# Revit family: RN 81041 Optipress-Aquaplus-Vis de rappel
name_source: partatom
category: Rohrformteile
units: mm (PartAtom-declared; Revit-internal decimal feet)

## family parameters
Arbeitsebenenbasiert = Nein
Beim Laden mit Abzugskörper schneiden = Nein
Bemaßung runder Anschluss = Durchmesser verwenden
Gemeinsam genutzt = Nein
Immer vertikal = Ja
Teiletyp = Verbindung

## types (7) — shared parameters
1.010.00.2 Numéro de feuille de la directive = 29
1.010.00.3 Date de publication (mois) de la ligne directrice = 201308
1.010.00.4 Nom du Fabricant = R. Nussbaum AG
1.010.00.5 Date de révision du fichier = 20190521
1.010.00.6 Adresse Web du fabricant = http://www.nussbaum.ch
1.100.00.4 Désignation du produit = Alimentation
1.110.00.2 Indice = 4
1.110.00.4 Désignation du produit = Optipress
1.960/3L.00.8 Lien (URL) = https://www.nussbaum.ch
29.700.00.4 Nom du produit = Optipress-Aquaplus-Vis de rappel
29.700.00.5 Identification du produit = 2
29.700.00.6 Forme transversale = 1
29.700.00.7 Système de taille nominale = DN
29.700.00.8 Système de pression nominale = PN
29.710.02.4 Pression nominale = 16
29.710.02.5 Max. [hPa] = 1600
29.710.02.7 Max. [hPa] = 1600
29.710.02.9 Max. [°C] = 95
Connector Visibility = Nein
EnclosingSpace Visibility = Nein

## per-type parameters (varying)
| type | 1.800.00.3 Numéro BS | 1.810.00.3 Numéro de commande fabricant | 1.810.00.4 Numéro DATANORM | 1.810.00.5 Numéro StLB | 1.810.00.6 Numéro GTIN | 29.710.02.10 Poids d'ajustement [kg] | 29.710.02.3 La désignation | CONNECTOR0_DIAMETER_dX_0r | CONNECTOR0_dX_01 | CONNECTOR0_ref_dX | CONNECTOR1_DIAMETER_dX_0r | CONNECTOR1_dX_00 | CONNECTOR1_dX_01 | CONNECTOR1_ref_dX | R. Nussbaum AG 81041.22 fr Visibility | R. Nussbaum AG 81041.23 fr Visibility | R. Nussbaum AG 81041.24 fr Visibility | R. Nussbaum AG 81041.25 fr Visibility | R. Nussbaum AG 81041.26 fr Visibility | R. Nussbaum AG 81041.27 fr Visibility | R. Nussbaum AG 81041.28 fr Visibility |
| 81041.22, Optipress-Aquaplus-Vis de rappel, DN=12, L=82 | 01900400000000000000000000000000000000000000000026000000000000000008 | 81041.22 | 81041.22 | 266.312 | 7612945021984 | 0.191 | Optipress-Aquaplus-Vis de rappel, DN=12, L=82 | 12 mm  [stored 0.0393701 ft] | 22 mm | 22 mm | 12 mm  [stored 0.0393701 ft] | 53 mm | 75 mm | 53 mm | Ja | Nein | Nein | Nein | Nein | Nein | Nein |
| 81041.23, Optipress-Aquaplus-Vis de rappel, DN=15, L=85 | 01900400000000000000000000000000000000000000000026000000000000000009 | 81041.23 | 81041.23 | 266.313 | 7612945021991 | 0.152 | Optipress-Aquaplus-Vis de rappel, DN=15, L=85 | 15 mm  [stored 0.0492126 ft] | 22 mm | 22 mm | 15 mm  [stored 0.0492126 ft] | 56 mm | 78 mm | 56 mm | Nein | Ja | Nein | Nein | Nein | Nein | Nein |
| 81041.24, Optipress-Aquaplus-Vis de rappel, DN=20, L=91 | 01900400000000000000000000000000000000000000000026000000000000000010 | 81041.24 | 81041.24 | 266.314 | 7612945022004 | 0.229 | Optipress-Aquaplus-Vis de rappel, DN=20, L=91 | 20 mm | 24 mm | 24 mm | 20 mm | 62 mm | 86 mm | 62 mm | Nein | Nein | Ja | Nein | Nein | Nein | Nein |
| 81041.25, Optipress-Aquaplus-Vis de rappel, DN=25, L=100 | 01900400000000000000000000000000000000000000000026000000000000000011 | 81041.25 | 81041.25 | 266.315 | 7612945022011 | 0.315 | Optipress-Aquaplus-Vis de rappel, DN=25, L=100 | 25 mm  [stored 0.082021 ft] | 24 mm | 24 mm | 25 mm  [stored 0.082021 ft] | 71 mm | 95 mm | 71 mm | Nein | Nein | Nein | Ja | Nein | Nein | Nein |
| 81041.26, Optipress-Aquaplus-Vis de rappel, DN=32, L=108 | 01900400000000000000000000000000000000000000000026000000000000000012 | 81041.26 | 81041.26 | 266.316 | 7612945022028 | 0.425 | Optipress-Aquaplus-Vis de rappel, DN=32, L=108 | 32 mm | 26 mm | 26 mm | 32 mm | 74 mm | 100 mm  [stored 0.328084 ft] | 74 mm | Nein | Nein | Nein | Nein | Ja | Nein | Nein |
| 81041.27, Optipress-Aquaplus-Vis de rappel, DN=40, L=131 | 01900400000000000000000000000000000000000000000026000000000000000013 | 81041.27 | 81041.27 | 266.317 | 7612945022035 | 0.667 | Optipress-Aquaplus-Vis de rappel, DN=40, L=131 | 40 mm | 36 mm | 36 mm | 40 mm | 85 mm | 121 mm | 85 mm | Nein | Nein | Nein | Nein | Nein | Ja | Nein |
| 81041.28, Optipress-Aquaplus-Vis de rappel, DN=50, L=141 | 01900400000000000000000000000000000000000000000026000000000000000014 | 81041.28 | 81041.28 | 266.318 | 7612945022042 | 1.015 | Optipress-Aquaplus-Vis de rappel, DN=50, L=141 | 50 mm | 40 mm | 40 mm | 50 mm | 89 mm | 129 mm | 89 mm | Nein | Nein | Nein | Nein | Nein | Nein | Ja |

note: column(s) folded — value = type name in every type: 1.800.00.4 Champ de commentaires

note: [stored X ft] marks values corroborated as IEEE doubles in the binary element streams (Revit-internal decimal feet)

## geometry (parser evidence)
native form markers: Sweep x2
no freeform markers — native parametric forms only
